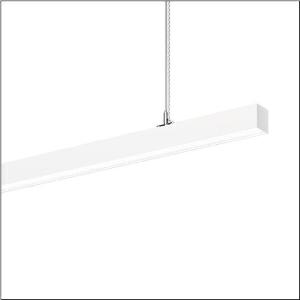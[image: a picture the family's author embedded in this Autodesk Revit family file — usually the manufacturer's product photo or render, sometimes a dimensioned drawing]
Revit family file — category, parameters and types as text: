
# Revit family: silica_r__21_51mx30db35wb_0444
name_source: partatom
category: Lighting Fixtures
units: mm (PartAtom-declared; Revit-internal decimal feet)

## family parameters
Cut with Voids When Loaded = No
Host = Face
Light Source = No
Part Type = Normal
Room Calculation Point = No
Round Connector Dimension = Use Diameter
Shared = No

## types (1)
- --- (1 x LED, 5260 lm, 34.1 W, 3000K)
    Apparent Load = 34 VA
    CIE Flux Codes = 47 79 96 57 100
    Color Rendering = 80
    Color Temperature = 3000K
    Default Elevation = 1800 mm
    Description = Silica® 21, office luminaire, primary optical cover: cover, of PMMA, opal, light emission: direct/indirect distribution, primary light characteristic: symmetric, installation type: suspended mounting, LED, rated luminous flux: 5.260lm, luminous efficacy: 154lm/W, light colour: 830, colour temperature: 3000K, with terminal, 3+2-pole, max. 2.5mm², mains connection: 220..240V, AC, 50/60Hz, rated input power: 34.1W, luminaire housing, of aluminium, traffic white (RAL 9016), length: 1.504mm, width: 53mm, height: 53mm, protection rating (complete): IP20, insulation class (complete): insulation class I (protective earthing), certification: CE, permissible operating ambient temperature: 0..+35°C, standard: EN 50419, packaging unit: 1 piece
    Height = 53 mm
    Lamp = 1 x LED
    Lamp Light Flux = 5260 lm
    Lamp Power = 34.1 W
    Lamp count = 1
    Length = 1504 mm
    Luminous efficacy = 154 lm/W
    Manufacturer = Siteco
    ModVariant = No
    Model = 51MX30DB35WB
    Mounting Place = Ceiling
    Mounting Type = Pendant
    Number of Poles = 1
    OnlyDefault = Yes
    Power Factor = 1
    Product Name = Silica® 21
    Product group = office luminaire | ceiling pendant
    ProductGroupID = 902
    Protection Class = Protection class I
    Protection Degree = IP 20
    RLX_Detail_Level = 1
    RLX_Emergency_Light_Flux = 0 lm
    RLX_Emergency_Type = 0
    RLX_Emergency_Type_DB = No
    RlxData = <blob elided: 21529 chars, md5=613892b9>
    Socket = socket
    Standby Power = 0 W
    System Light Flux = 5260 lm
    System Power = 34 W
    Type Comments = factory setting: luminous flux: 100 % | dim-lin: 254 | 233 mA
    Type Image = l_1335916.jpg
    URL = http://relux.com
    VarID = @adj_085699
    Voltage = 0 V
    Weight = 0.00 kg
    Width = 53 mm

## geometry (parser evidence)
native form markers: Blend x4, Sweep x13
no freeform markers — native parametric forms only
